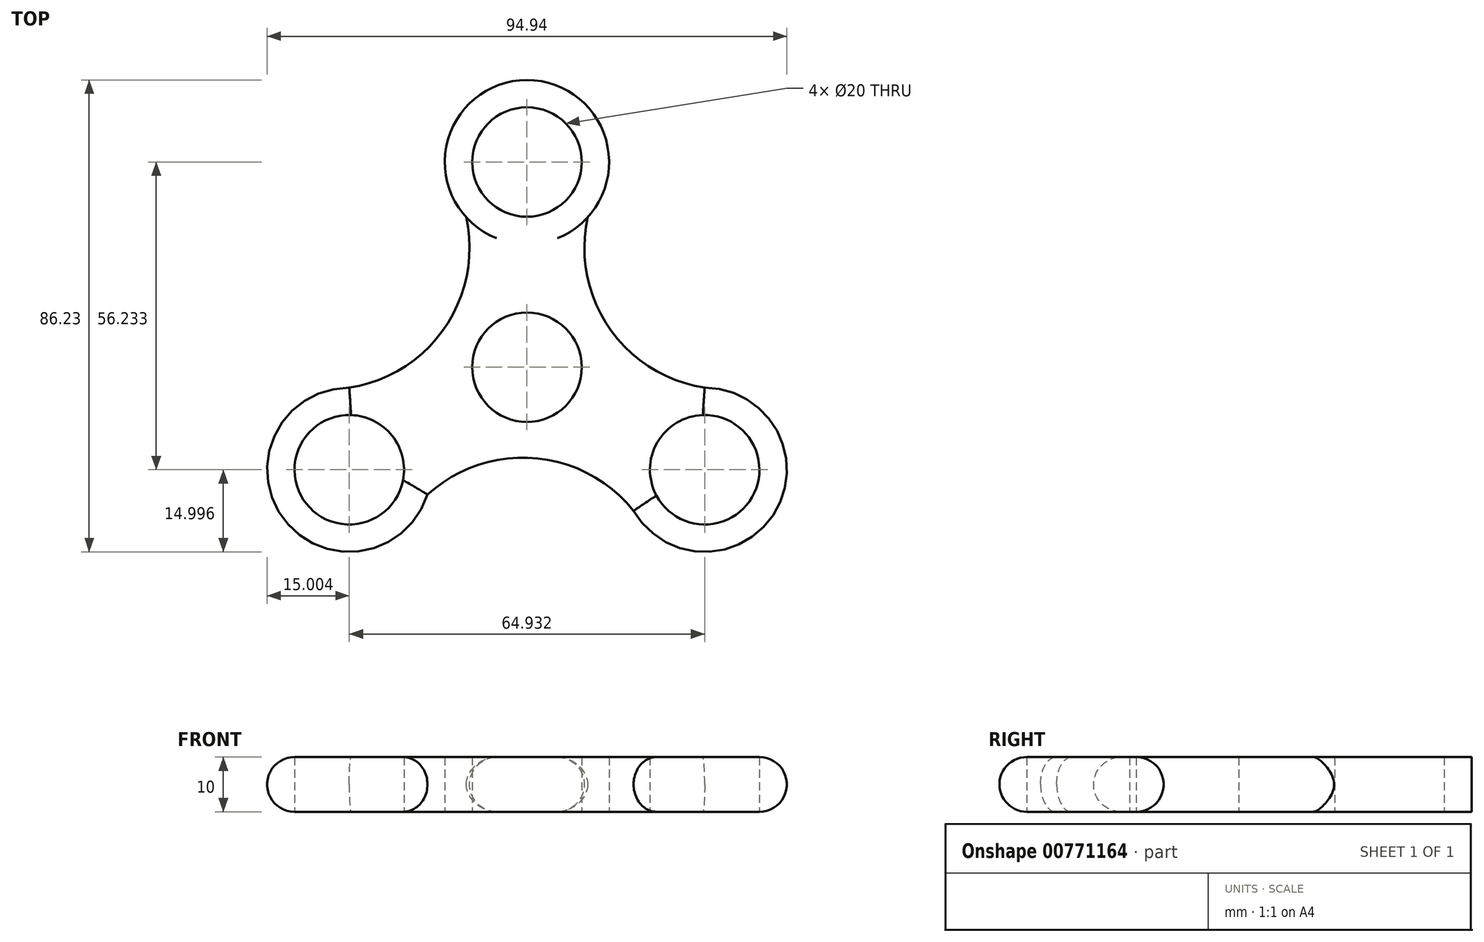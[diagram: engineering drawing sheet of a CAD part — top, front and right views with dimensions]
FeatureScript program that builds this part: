
annotation { "Feature Type Name" : "Feature", "Feature Type Description" : "" }
export const myFeature = defineFeature(function(context is Context, id is Id, definition is map)
    precondition{}
    {
        {
            var Q0;
            Q0=qCreatedBy(makeId("Top.planeOp"),FACE);
            var sketch = newSketch(context, id + "F0", { "sketchPlane" : qUnion([Q0])});
            skCircle(sketch, "E0", {"center": v(0, 0) * mm, "radius": 10 * mm});
            skLineSegment(sketch, "E1.0", {"start": v(32.47, -18.74) * mm, "end": v(22.47, -18.74) * mm});
            skPoint(sketch, "E1.0.midPoint", {"position": v(0, -18.74) * mm});
            skLineSegment(sketch, "E2", {"start": v(0, 0) * mm, "end": v(-32.47, -18.74) * mm, "construction": true});
            skLineSegment(sketch, "E3", {"start": v(0, 0) * mm, "end": v(32.47, -18.74) * mm, "construction": true});
            skLineSegment(sketch, "E4", {"start": v(0, 0) * mm, "end": v(0, 37.49) * mm, "construction": true});
            skCircle(sketch, "E5", {"center": v(0, 37.49) * mm, "radius": 10 * mm});
            skCircle(sketch, "E6", {"center": v(32.47, -18.74) * mm, "radius": 10 * mm});
            skCircle(sketch, "E7", {"center": v(-32.47, -18.74) * mm, "radius": 10 * mm});
            skLineSegment(sketch, "E8.trimOffspring", {"start": v(27.47, -10.08) * mm, "end": v(32.47, -18.74) * mm});
            skCircle(sketch, "E9", {"center": v(0, 37.49) * mm, "radius": 15 * mm});
            skCircle(sketch, "E10.MirrorC", {"center": v(32.47, -18.74) * mm, "radius": 15 * mm});
            skCircle(sketch, "E11.MirrorC", {"center": v(-32.47, -18.74) * mm, "radius": 15 * mm});
            skArc(sketch, "E12", {"start": v(-32.47, -3.74) * mm, "mid": v(-15.03, 7.19) * mm, "end": v(-11.09, 27.39) * mm});
            skArc(sketch, "E13.MirrorCS", {"start": v(32.47, -3.74) * mm, "mid": v(15.03, 7.19) * mm, "end": v(11.09, 27.39) * mm});
            skArc(sketch, "E14.MirrorCS", {"start": v(19.48, -26.24) * mm, "mid": v(1.29, -16.61) * mm, "end": v(-18.17, -23.3) * mm});
            skSolve(sketch);
        }
        {
            var Q0;
            Q0=makeQuery(id+"F0.imprint","IMPRINT",FACE,{"disambiguationData":[TD([[makeQuery(id+"F0.imprint","IMPRINT",EDGE,{"derivedFrom":sQuery(id+"F0.wireOp",EDGE,"E5")}),-1.0]])]});
            var Q1;
            Q1=makeQuery(id+"F0.imprint","IMPRINT",FACE,{"disambiguationData":[TD([[makeQuery(id+"F0.imprint","IMPRINT",EDGE,{"derivedFrom":sQuery(id+"F0.wireOp",EDGE,"E7")}),-1.0]])]});
            var Q2;
            {var subQ0=sQuery(id+"F0.wireOp",EDGE,"E6");var subQ1=makeQuery(id+"F0.imprint","INTERSECT",VERTEX,{"derivedFrom":[sQuery(id+"F0.wireOp",EDGE,"E1.0"),subQ0]});Q2=makeQuery(id+"F0.imprint","IMPRINT",FACE,{"disambiguationData":[TD([[makeQuery(id+"F0.imprint","IMPRINT",EDGE,{"disambiguationData":[TD([[subQ1,1.0]])],"derivedFrom":subQ0}),-1.0]])]});}
            var Q3;
            Q3=makeQuery(id+"F0.imprint","IMPRINT",FACE,{"disambiguationData":[TD([[makeQuery(id+"F0.imprint","IMPRINT",EDGE,{"derivedFrom":sQuery(id+"F0.wireOp",EDGE,"E0")}),-1.0]])]});
            extrude(context, id + "F1", {"entities" : qUnion([Q0, Q1, Q2, Q3]), "depth" : 10 * mm, "offsetDistance" : 25 * mm});
        }
        {
            var Q0;
            Q0=makeQuery(id+"F1.opExtrude","CAP_EDGE",EDGE,{"disambiguationData":[OSD([sQuery(id+"F0.wireOp",EDGE,"E12")])],"isStart":true});
            var Q1;
            Q1=makeQuery(id+"F1.opExtrude","CAP_EDGE",EDGE,{"disambiguationData":[OSD([sQuery(id+"F0.wireOp",EDGE,"E9")])],"isStart":true});
            var Q2;
            Q2=makeQuery(id+"F1.opExtrude","CAP_EDGE",EDGE,{"disambiguationData":[OSD([sQuery(id+"F0.wireOp",EDGE,"E13.MirrorCS")])],"isStart":true});
            var Q3;
            Q3=makeQuery(id+"F1.opExtrude","CAP_EDGE",EDGE,{"disambiguationData":[OSD([sQuery(id+"F0.wireOp",EDGE,"E10.MirrorC")])],"isStart":true});
            var Q4;
            Q4=makeQuery(id+"F1.opExtrude","CAP_EDGE",EDGE,{"disambiguationData":[OSD([sQuery(id+"F0.wireOp",EDGE,"E14.MirrorCS")])],"isStart":true});
            var Q5;
            Q5=makeQuery(id+"F1.opExtrude","CAP_EDGE",EDGE,{"disambiguationData":[OSD([sQuery(id+"F0.wireOp",EDGE,"E11.MirrorC")])],"isStart":true});
            var Q6;
            Q6=makeQuery(id+"F1.opExtrude","CAP_EDGE",EDGE,{"disambiguationData":[OSD([sQuery(id+"F0.wireOp",EDGE,"E10.MirrorC")])],"isStart":false});
            var Q7;
            Q7=makeQuery(id+"F1.opExtrude","CAP_EDGE",EDGE,{"disambiguationData":[OSD([sQuery(id+"F0.wireOp",EDGE,"E13.MirrorCS")])],"isStart":false});
            var Q8;
            Q8=makeQuery(id+"F1.opExtrude","CAP_EDGE",EDGE,{"disambiguationData":[OSD([sQuery(id+"F0.wireOp",EDGE,"E14.MirrorCS")])],"isStart":false});
            var Q9;
            Q9=makeQuery(id+"F1.opExtrude","CAP_EDGE",EDGE,{"disambiguationData":[OSD([sQuery(id+"F0.wireOp",EDGE,"E12")])],"isStart":false});
            var Q10;
            Q10=makeQuery(id+"F1.opExtrude","CAP_EDGE",EDGE,{"disambiguationData":[OSD([sQuery(id+"F0.wireOp",EDGE,"E9")])],"isStart":false});
            var Q11;
            Q11=makeQuery(id+"F1.opExtrude","CAP_EDGE",EDGE,{"disambiguationData":[OSD([sQuery(id+"F0.wireOp",EDGE,"E11.MirrorC")])],"isStart":false});
            fillet(context, id + "F2", {"entities" : qUnion([Q0, Q1, Q2, Q3, Q4, Q5, Q6, Q7, Q8, Q9, Q10, Q11]), "radius" : 5 * mm, "tangentPropagation" : true, "allowEdgeOverflow" : false});
        }
    });
